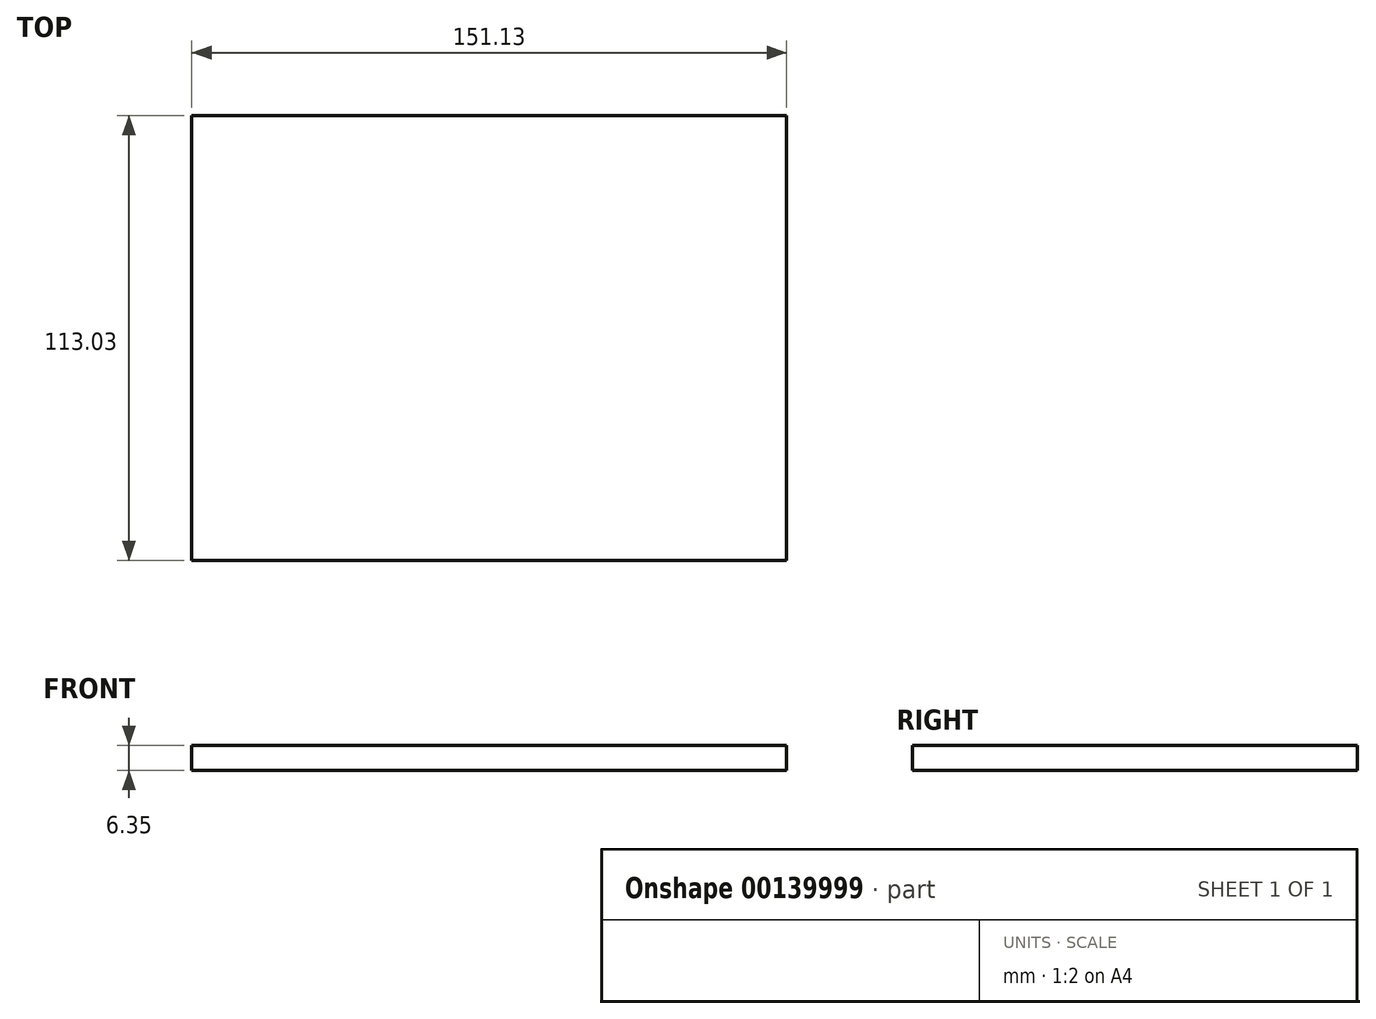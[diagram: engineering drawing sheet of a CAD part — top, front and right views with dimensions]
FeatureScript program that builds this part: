
annotation { "Feature Type Name" : "Feature", "Feature Type Description" : "" }
export const myFeature = defineFeature(function(context is Context, id is Id, definition is map)
    precondition{}
    {
        {
            var Q0;
            Q0=qCreatedBy(makeId("Top.planeOp"),FACE);
            var sketch = newSketch(context, id + "F0", { "sketchPlane" : qUnion([Q0])});
            skLineSegment(sketch, "E0.bottom", {"start": v(-77.03, 51.72) * mm, "end": v(74.1, 51.72) * mm});
            skLineSegment(sketch, "E0.top", {"start": v(-77.03, -61.31) * mm, "end": v(74.1, -61.31) * mm});
            skLineSegment(sketch, "E0.left", {"start": v(-77.03, 51.72) * mm, "end": v(-77.03, -61.31) * mm});
            skLineSegment(sketch, "E0.right", {"start": v(74.1, 51.72) * mm, "end": v(74.1, -61.31) * mm});
            skSolve(sketch);
        }
        {
            var Q0;
            Q0=makeQuery(id+"F0.imprint","IMPRINT",FACE,{"disambiguationData":[TD([[makeQuery(id+"F0.imprint","IMPRINT",EDGE,{"derivedFrom":sQuery(id+"F0.wireOp",EDGE,"E0.bottom")}),-1.0]])]});
            extrude(context, id + "F1", {"entities" : qUnion([Q0]), "depth" : 6.35 * mm});
        }
    });
